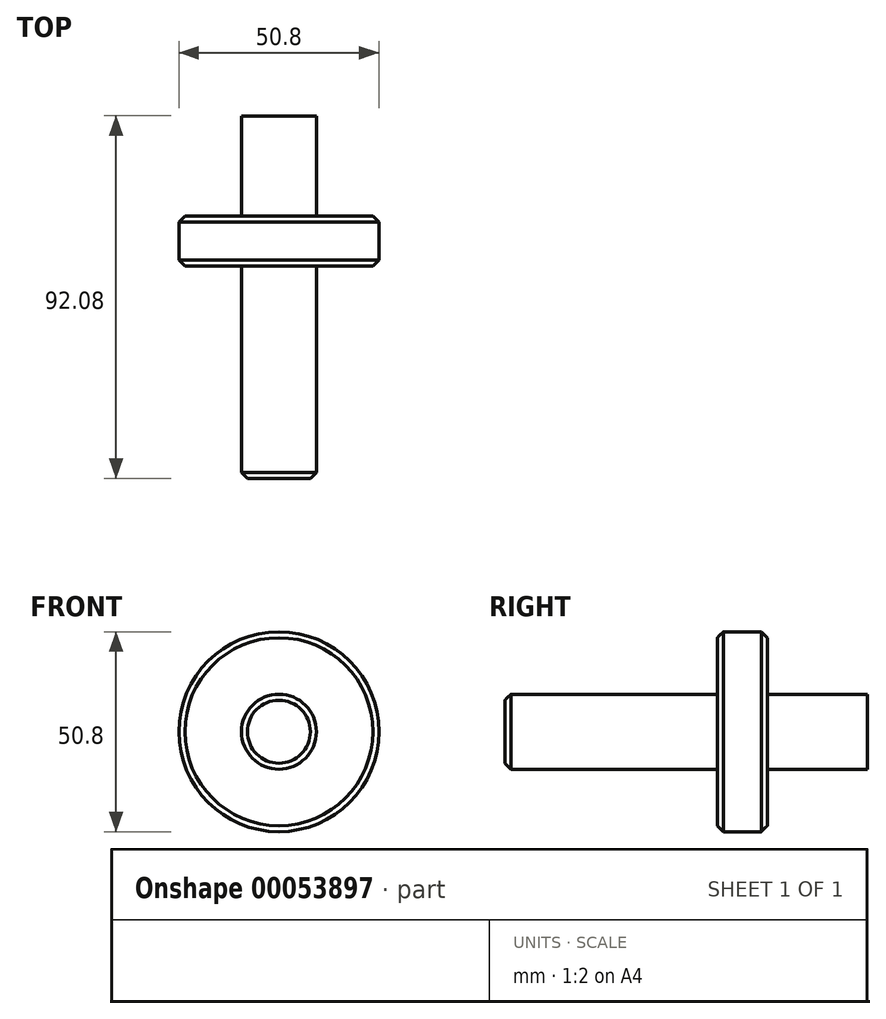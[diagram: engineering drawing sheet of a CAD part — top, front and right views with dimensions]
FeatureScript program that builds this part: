
annotation { "Feature Type Name" : "Feature", "Feature Type Description" : "" }
export const myFeature = defineFeature(function(context is Context, id is Id, definition is map)
    precondition{}
    {
        {
            var Q0;
            Q0=qCreatedBy(makeId("Right.planeOp"),FACE);
            var sketch = newSketch(context, id + "F0", { "sketchPlane" : qUnion([Q0])});
            skLineSegment(sketch, "E0", {"start": v(0, 9.52) * mm, "end": v(53.98, 9.52) * mm});
            skLineSegment(sketch, "E1", {"start": v(53.98, 9.53) * mm, "end": v(53.98, 25.4) * mm});
            skLineSegment(sketch, "E2", {"start": v(53.98, 25.4) * mm, "end": v(66.67, 25.4) * mm});
            skLineSegment(sketch, "E3", {"start": v(66.67, 25.4) * mm, "end": v(66.67, 9.53) * mm});
            skLineSegment(sketch, "E4", {"start": v(66.67, 9.53) * mm, "end": v(92.08, 9.53) * mm});
            skLineSegment(sketch, "E5", {"start": v(92.08, 9.53) * mm, "end": v(92.08, 0) * mm});
            skLineSegment(sketch, "E6", {"start": v(92.08, 0) * mm, "end": v(0, 0) * mm});
            skLineSegment(sketch, "E7", {"start": v(0, 0) * mm, "end": v(0, 9.52) * mm});
            skLineSegment(sketch, "E8", {"start": v(0, 0) * mm, "end": v(-18.44, 0) * mm, "construction": true});
            skLineSegment(sketch, "E9", {"start": v(25.4, 9.53) * mm, "end": v(25.4, 12.7) * mm, "construction": true});
            skLineSegment(sketch, "E10", {"start": v(50.8, 12.7) * mm, "end": v(50.8, 19.05) * mm, "construction": true});
            skLineSegment(sketch, "E11", {"start": v(50.8, 19.05) * mm, "end": v(53.98, 19.05) * mm, "construction": true});
            skLineSegment(sketch, "E12", {"start": v(53.98, 25.4) * mm, "end": v(53.98, 19.05) * mm, "construction": true});
            skLineSegment(sketch, "E13", {"start": v(50.8, 12.7) * mm, "end": v(25.4, 12.7) * mm, "construction": true});
            skSolve(sketch);
        }
        {
            var Q0;
            Q0 = qSketchRegion(id + "F0", true);
            var Q1;
            Q1=sQuery(id+"F0.wireOp",EDGE,"E8");
            revolve(context, id + "F1", {"entities" : qUnion([Q0]), "axis" : qUnion([Q1]), "revolveType" : RevolveType.FULL});
        }
        {
            var Q0;
            Q0=makeQuery(id+"F1.opRevolve","SWEPT_EDGE",EDGE,{"disambiguationData":[OSD([sQuery(id+"F0.wireOp",EDGE,"E1"),sQuery(id+"F0.wireOp",EDGE,"E2")])]});
            var Q1;
            Q1=makeQuery(id+"F1.opRevolve","SWEPT_EDGE",EDGE,{"disambiguationData":[OSD([sQuery(id+"F0.wireOp",EDGE,"E2"),sQuery(id+"F0.wireOp",EDGE,"E3")])]});
            var Q2;
            Q2=makeQuery(id+"F1.opRevolve","SWEPT_EDGE",EDGE,{"disambiguationData":[OSD([sQuery(id+"F0.wireOp",EDGE,"E0"),sQuery(id+"F0.wireOp",EDGE,"E7")])]});
            chamfer(context, id + "F2", {"entities" : qUnion([Q0, Q1, Q2]), "width" : 1.52 * mm, "tangentPropagation" : true});
        }
    });
